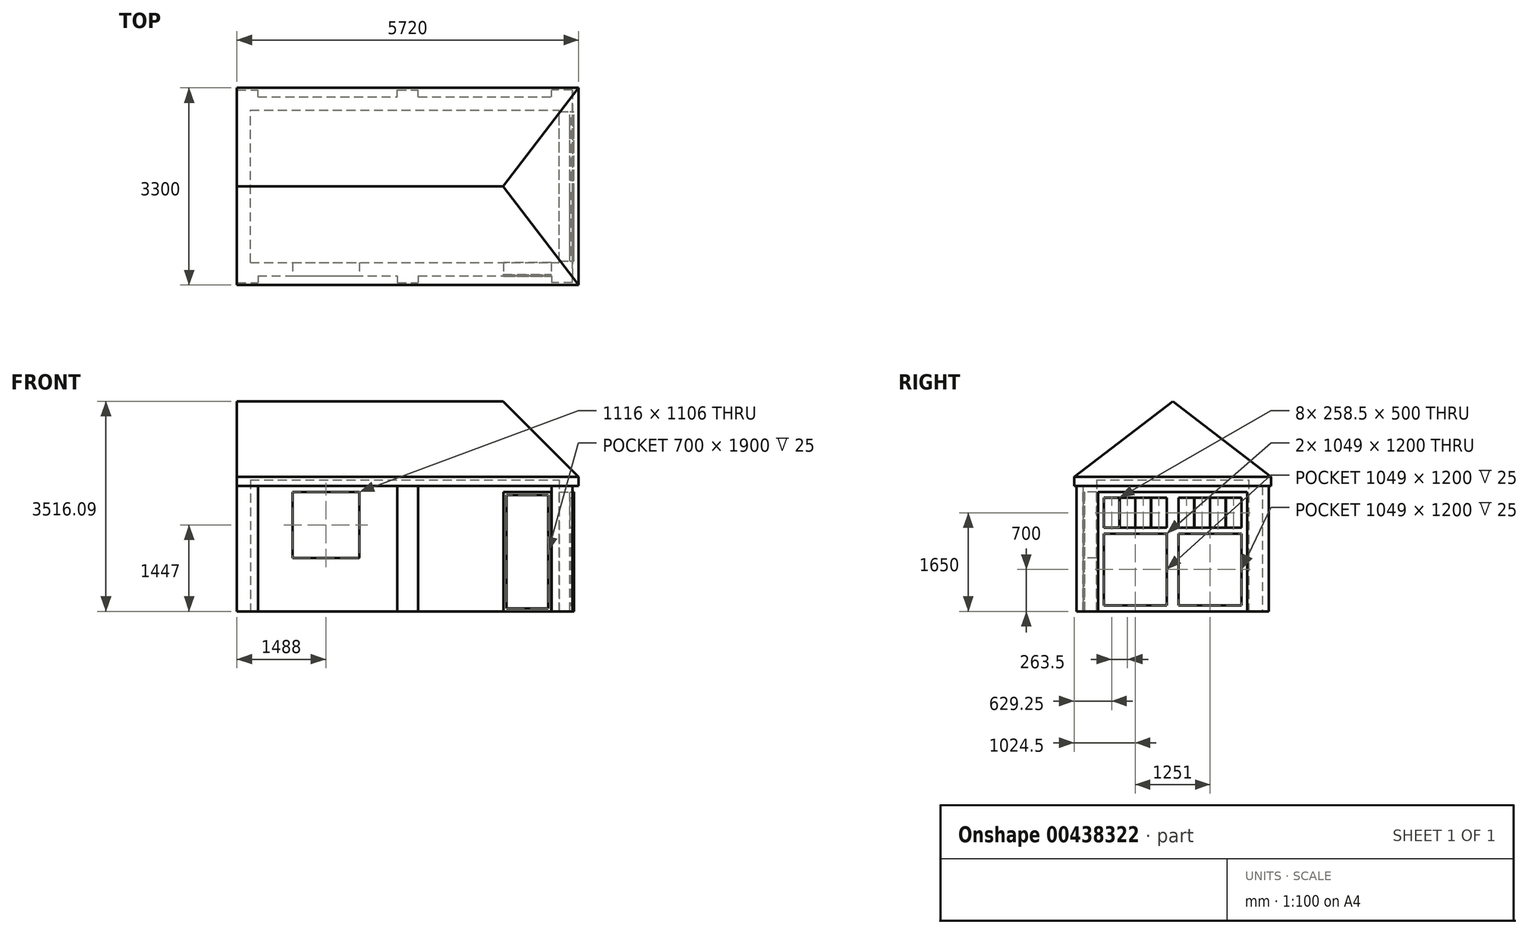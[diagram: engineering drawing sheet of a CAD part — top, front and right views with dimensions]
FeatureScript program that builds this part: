
annotation { "Feature Type Name" : "Feature", "Feature Type Description" : "" }
export const myFeature = defineFeature(function(context is Context, id is Id, definition is map)
    precondition{}
    {
        {
            var Q0;
            Q0=qCreatedBy(makeId("Top.planeOp"),FACE);
            var sketch = newSketch(context, id + "F0", { "sketchPlane" : qUnion([Q0])});
            skLineSegment(sketch, "E0.bottom", {"start": v(0, 0) * mm, "end": v(5620, 0) * mm});
            skLineSegment(sketch, "E0.top", {"start": v(0, 3000) * mm, "end": v(5620, 3000) * mm});
            skLineSegment(sketch, "E0.left", {"start": v(0, 0) * mm, "end": v(0, 3000) * mm});
            skLineSegment(sketch, "E0.right", {"start": v(5620, 0) * mm, "end": v(5620, 3000) * mm});
            skLineSegment(sketch, "E1.bottom", {"start": v(225, 225) * mm, "end": v(5395, 225) * mm});
            skLineSegment(sketch, "E1.top", {"start": v(225, 2775) * mm, "end": v(5395, 2775) * mm});
            skLineSegment(sketch, "E1.left", {"start": v(225, 225) * mm, "end": v(225, 2775) * mm});
            skLineSegment(sketch, "E1.right", {"start": v(5395, 225) * mm, "end": v(5395, 2775) * mm});
            skSolve(sketch);
        }
        {
            var Q0;
            Q0 = qSketchRegion(id + "F0", true);
            extrude(context, id + "F1", {"entities" : qUnion([Q0]), "depth" : 2200 * mm, "offsetDistance" : 25 * mm});
        }
        {
            var Q0;
            Q0=makeQuery(id+"F1.opExtrude","SWEPT_FACE",FACE,{"disambiguationData":[OSD([sQuery(id+"F0.wireOp",EDGE,"E0.right")])]});
            var sketch = newSketch(context, id + "F2", { "sketchPlane" : qUnion([Q0])});
            skLineSegment(sketch, "E2.bottom", {"start": v(250, 0) * mm, "end": v(2750, 0) * mm});
            skLineSegment(sketch, "E2.top", {"start": v(250, 2000) * mm, "end": v(2750, 2000) * mm});
            skLineSegment(sketch, "E2.left", {"start": v(250, 0) * mm, "end": v(250, 2000) * mm});
            skLineSegment(sketch, "E2.right", {"start": v(2750, 0) * mm, "end": v(2750, 2000) * mm});
            skSolve(sketch);
        }
        {
            var Q0;
            Q0 = qSketchRegion(id + "F2", true);
            extrude(context, id + "F3", {"entities" : qUnion([Q0]), "operationType" : NewBodyOperationType.REMOVE, "endBound" : BoundingType.UP_TO_NEXT, "oppositeDirection" : true, "depth" : 25 * mm, "offsetDistance" : 25 * mm});
        }
        {
            var Q0;
            Q0=makeQuery(id+"F1.opExtrude","SWEPT_FACE",FACE,{"disambiguationData":[OSD([sQuery(id+"F0.wireOp",EDGE,"E0.bottom")])]});
            var sketch = newSketch(context, id + "F4", { "sketchPlane" : qUnion([Q0])});
            skLineSegment(sketch, "E3.bottom", {"start": v(930, 2000) * mm, "end": v(2046, 2000) * mm});
            skLineSegment(sketch, "E3.top", {"start": v(930, 894) * mm, "end": v(2046, 894) * mm});
            skLineSegment(sketch, "E3.left", {"start": v(930, 2000) * mm, "end": v(930, 894) * mm});
            skLineSegment(sketch, "E3.right", {"start": v(2046, 2000) * mm, "end": v(2046, 894) * mm});
            skLineSegment(sketch, "E4.bottom", {"start": v(5260, 0) * mm, "end": v(4460, 0) * mm});
            skLineSegment(sketch, "E4.top", {"start": v(5260, 2000) * mm, "end": v(4460, 2000) * mm});
            skLineSegment(sketch, "E4.left", {"start": v(5260, 0) * mm, "end": v(5260, 2000) * mm});
            skLineSegment(sketch, "E4.right", {"start": v(4460, 0) * mm, "end": v(4460, 2000) * mm});
            skSolve(sketch);
        }
        {
            var Q0;
            Q0 = qSketchRegion(id + "F4", true);
            extrude(context, id + "F5", {"entities" : qUnion([Q0]), "operationType" : NewBodyOperationType.REMOVE, "endBound" : BoundingType.UP_TO_NEXT, "oppositeDirection" : true, "depth" : 25 * mm, "offsetDistance" : 25 * mm});
        }
        {
            var Q0;
            Q0=makeQuery(id+"F1.opExtrude","SWEPT_FACE",FACE,{"disambiguationData":[OSD([sQuery(id+"F0.wireOp",EDGE,"E0.bottom")])]});
            cPlane(context, id + "F6", {"entities" : qUnion([Q0]), "cplaneType" : CPlaneType.OFFSET, "offset" : 25 * mm, "oppositeDirection" : true, "width" : 150 * mm, "height" : 150 * mm});
        }
        {
            var Q0;
            Q0=qCreatedBy(id+"F6.planeOp",FACE);
            var sketch = newSketch(context, id + "F7", { "sketchPlane" : qUnion([Q0])});
            skLineSegment(sketch, "E5.bottom", {"start": v(4510, 1950) * mm, "end": v(5210, 1950) * mm});
            skLineSegment(sketch, "E5.top", {"start": v(4510, 50) * mm, "end": v(5210, 50) * mm});
            skLineSegment(sketch, "E5.left", {"start": v(4510, 1950) * mm, "end": v(4510, 50) * mm});
            skLineSegment(sketch, "E5.right", {"start": v(5210, 1950) * mm, "end": v(5210, 50) * mm});
            skLineSegment(sketch, "E6.bottom", {"start": v(4460, 2000) * mm, "end": v(5260, 2000) * mm});
            skLineSegment(sketch, "E6.top", {"start": v(4460, 0) * mm, "end": v(5260, 0) * mm});
            skLineSegment(sketch, "E6.left", {"start": v(4460, 2000) * mm, "end": v(4460, 0) * mm});
            skLineSegment(sketch, "E6.right", {"start": v(5260, 2000) * mm, "end": v(5260, 0) * mm});
            skSolve(sketch);
        }
        {
            var Q0;
            Q0 = qSketchRegion(id + "F7", true);
            extrude(context, id + "F8", {"entities" : qUnion([Q0]), "depth" : 30 * mm, "offsetDistance" : 25 * mm});
        }
        {
            var Q0;
            Q0=makeQuery(id+"F7.imprint","IMPRINT",FACE,{"disambiguationData":[TD([[makeQuery(id+"F7.imprint","IMPRINT",EDGE,{"derivedFrom":sQuery(id+"F7.wireOp",EDGE,"E5.bottom")}),-1.0]])]});
            extrude(context, id + "F9", {"entities" : qUnion([Q0]), "operationType" : NewBodyOperationType.ADD, "depth" : 5 * mm, "offsetDistance" : 25 * mm});
        }
        {
            var Q0;
            Q0=makeQuery(id+"F1.opExtrude","SWEPT_FACE",FACE,{"disambiguationData":[OSD([sQuery(id+"F0.wireOp",EDGE,"E0.right")])]});
            var sketch = newSketch(context, id + "F10", { "sketchPlane" : qUnion([Q0])});
            skLineSegment(sketch, "E7", {"start": v(0, 2100) * mm, "end": v(-150, 2100) * mm});
            skLineSegment(sketch, "E8", {"start": v(-150, 2100) * mm, "end": v(-150, 2250) * mm});
            skLineSegment(sketch, "E9", {"start": v(-150, 2250) * mm, "end": v(1500, 3516.09) * mm});
            skLineSegment(sketch, "E10", {"start": v(1500, 3516.09) * mm, "end": v(3150, 2250) * mm});
            skLineSegment(sketch, "E11", {"start": v(3150, 2250) * mm, "end": v(3150, 2100) * mm});
            skLineSegment(sketch, "E12", {"start": v(3150, 2100) * mm, "end": v(3000, 2100) * mm});
            skLineSegment(sketch, "E13", {"start": v(3000, 2100) * mm, "end": v(3000, 2200) * mm});
            skLineSegment(sketch, "E14", {"start": v(3000, 2200) * mm, "end": v(0, 2200) * mm});
            skLineSegment(sketch, "E15", {"start": v(0, 2200) * mm, "end": v(0, 2100) * mm});
            skSolve(sketch);
        }
        {
            var Q0;
            Q0 = qSketchRegion(id + "F10", true);
            var Q1;
            Q1=makeQuery(id+"F1.opExtrude","SWEPT_FACE",FACE,{"disambiguationData":[OSD([sQuery(id+"F0.wireOp",EDGE,"E0.left")])]});
            extrude(context, id + "F11", {"entities" : qUnion([Q0]), "operationType" : NewBodyOperationType.ADD, "endBound" : BoundingType.UP_TO_SURFACE, "oppositeDirection" : true, "depth" : 5630 * mm, "endBoundEntityFace" : qUnion([Q1]), "offsetDistance" : 100 * mm, "offsetOppositeDirection" : true, "hasSecondDirection" : true, "secondDirectionOppositeDirection" : false, "secondDirectionDepth" : 100 * mm});
        }
        {
            var Q0;
            {var subQ1=sQuery(id+"F10.wireOp",EDGE,"E14");Q0=makeQuery(id+"F11.boolean.opBoolean","SPLIT",FACE,{"disambiguationData":[TD([makeQuery(id+"F1.opExtrude","SWEPT_FACE",FACE,{"disambiguationData":[OSD([sQuery(id+"F0.wireOp",EDGE,"E0.right")])]})])],"derivedFrom":makeQuery(id+"F11.opExtrude","SWEPT_FACE",FACE,{"disambiguationData":[OSD([subQ1])]})});}
            var Q1;
            Q1=makeQuery(id+"F11.opExtrude","SWEPT_FACE",FACE,{"disambiguationData":[OSD([sQuery(id+"F10.wireOp",EDGE,"E7")])]});
            extrude(context, id + "F12", {"entities" : qUnion([Q0]), "operationType" : NewBodyOperationType.ADD, "endBound" : BoundingType.UP_TO_SURFACE, "depth" : 25 * mm, "endBoundEntityFace" : qUnion([Q1]), "offsetDistance" : 25 * mm});
        }
        {
            var Q0;
            Q0=makeQuery(id+"F11.opExtrude","SWEPT_FACE",FACE,{"disambiguationData":[OSD([sQuery(id+"F10.wireOp",EDGE,"E8")])]});
            var sketch = newSketch(context, id + "F13", { "sketchPlane" : qUnion([Q0])});
            skLineSegment(sketch, "E16", {"start": v(5720, 2250) * mm, "end": v(3720, 4250) * mm});
            skLineSegment(sketch, "E17", {"start": v(3720, 4250) * mm, "end": v(5720, 4250) * mm});
            skLineSegment(sketch, "E18", {"start": v(5720, 4250) * mm, "end": v(5720, 2250) * mm});
            skSolve(sketch);
        }
        {
            var Q0;
            Q0 = qSketchRegion(id + "F13", true);
            extrude(context, id + "F14", {"entities" : qUnion([Q0]), "operationType" : NewBodyOperationType.REMOVE, "oppositeDirection" : true, "depth" : 6760 * mm, "offsetDistance" : 25 * mm});
        }
        {
            var Q0;
            {var subQ0=sQuery(id+"F0.wireOp",EDGE,"E0.left");var subQ1=sQuery(id+"F0.wireOp",EDGE,"E0.top");var subQ2=sQuery(id+"F0.wireOp",EDGE,"E0.right");var subQ3=sQuery(id+"F0.wireOp",EDGE,"E0.bottom");var subQ4=sQuery(id+"F0.wireOp",EDGE,"E1.bottom");var subQ5=sQuery(id+"F0.wireOp",EDGE,"E1.top");var subQ6=sQuery(id+"F0.wireOp",EDGE,"E1.left");var subQ7=sQuery(id+"F0.wireOp",EDGE,"E1.right");Q0=makeQuery(id+"F5.boolean.opBoolean","SPLIT",FACE,{"disambiguationData":[TD([makeQuery(id+"F1.opExtrude","SWEPT_FACE",FACE,{"disambiguationData":[OSD([subQ1])]})])],"derivedFrom":makeQuery(id+"F1.opExtrude","CAP_FACE",FACE,{"disambiguationData":[OSD([subQ3,subQ1,subQ0,subQ2,subQ4,subQ5,subQ6,subQ7])],"isStart":true})});}
            var sketch = newSketch(context, id + "F15", { "sketchPlane" : qUnion([Q0])});
            skLineSegment(sketch, "E19.bottom", {"start": v(0, 0) * mm, "end": v(350, 0) * mm});
            skLineSegment(sketch, "E19.top", {"start": v(0, 110) * mm, "end": v(350, 110) * mm});
            skLineSegment(sketch, "E19.left", {"start": v(0, 0) * mm, "end": v(0, 110) * mm});
            skLineSegment(sketch, "E19.right", {"start": v(350, 0) * mm, "end": v(350, 110) * mm});
            skLineSegment(sketch, "E20.bottom", {"start": v(2685, 0) * mm, "end": v(3035, 0) * mm});
            skLineSegment(sketch, "E20.top", {"start": v(2685, 110) * mm, "end": v(3035, 110) * mm});
            skLineSegment(sketch, "E20.left", {"start": v(2685, 0) * mm, "end": v(2685, 110) * mm});
            skLineSegment(sketch, "E20.right", {"start": v(3035, 0) * mm, "end": v(3035, 110) * mm});
            skLineSegment(sketch, "E21.bottom", {"start": v(5620, 0) * mm, "end": v(5270, 0) * mm});
            skLineSegment(sketch, "E21.top", {"start": v(5620, 110) * mm, "end": v(5270, 110) * mm});
            skLineSegment(sketch, "E21.left", {"start": v(5620, 0) * mm, "end": v(5620, 110) * mm});
            skLineSegment(sketch, "E21.right", {"start": v(5270, 0) * mm, "end": v(5270, 110) * mm});
            skLineSegment(sketch, "E22.bottom", {"start": v(0, -3000) * mm, "end": v(350, -3000) * mm});
            skLineSegment(sketch, "E22.top", {"start": v(0, -3110) * mm, "end": v(350, -3110) * mm});
            skLineSegment(sketch, "E22.left", {"start": v(0, -3000) * mm, "end": v(0, -3110) * mm});
            skLineSegment(sketch, "E22.right", {"start": v(350, -3000) * mm, "end": v(350, -3110) * mm});
            skLineSegment(sketch, "E23.bottom", {"start": v(2685, -3000) * mm, "end": v(3035, -3000) * mm});
            skLineSegment(sketch, "E23.top", {"start": v(2685, -3110) * mm, "end": v(3035, -3110) * mm});
            skLineSegment(sketch, "E23.left", {"start": v(2685, -3000) * mm, "end": v(2685, -3110) * mm});
            skLineSegment(sketch, "E23.right", {"start": v(3035, -3000) * mm, "end": v(3035, -3110) * mm});
            skLineSegment(sketch, "E24.bottom", {"start": v(5620, -3000) * mm, "end": v(5270, -3000) * mm});
            skLineSegment(sketch, "E24.top", {"start": v(5620, -3110) * mm, "end": v(5270, -3110) * mm});
            skLineSegment(sketch, "E24.left", {"start": v(5620, -3000) * mm, "end": v(5620, -3110) * mm});
            skLineSegment(sketch, "E24.right", {"start": v(5270, -3000) * mm, "end": v(5270, -3110) * mm});
            skLineSegment(sketch, "E25", {"start": v(2860, 428.34) * mm, "end": v(2860, -3399.48) * mm, "construction": true});
            skSolve(sketch);
        }
        {
            var Q0;
            Q0 = qSketchRegion(id + "F15", true);
            var Q1;
            {var subQ0=sQuery(id+"F10.wireOp",EDGE,"E7");Q1=makeQuery(id+"F12.boolean.opBoolean","MERGE",FACE,{"derivedFrom":[makeQuery(id+"F11.opExtrude","SWEPT_FACE",FACE,{"disambiguationData":[OSD([subQ0])]}),makeQuery(id+"F11.opExtrude","SWEPT_FACE",FACE,{"disambiguationData":[OSD([sQuery(id+"F10.wireOp",EDGE,"E12")])]}),makeQuery(id+"F12.opExtrude","CAP_FACE",FACE,{"disambiguationData":[OSD([subQ0])],"isStart":false})]});}
            extrude(context, id + "F16", {"entities" : qUnion([Q0]), "operationType" : NewBodyOperationType.ADD, "endBound" : BoundingType.UP_TO_SURFACE, "oppositeDirection" : true, "depth" : 25 * mm, "endBoundEntityFace" : qUnion([Q1]), "offsetDistance" : 25 * mm});
        }
        {
            var Q0;
            Q0=makeQuery(id+"F16.boolean.opBoolean","MERGE",FACE,{"derivedFrom":[makeQuery(id+"F1.opExtrude","SWEPT_FACE",FACE,{"disambiguationData":[OSD([sQuery(id+"F0.wireOp",EDGE,"E0.right")])]}),makeQuery(id+"F16.opExtrude","SWEPT_FACE",FACE,{"disambiguationData":[OSD([sQuery(id+"F15.wireOp",EDGE,"E21.left")])]}),makeQuery(id+"F16.opExtrude","SWEPT_FACE",FACE,{"disambiguationData":[OSD([sQuery(id+"F15.wireOp",EDGE,"E24.left")])]})]});
            var sketch = newSketch(context, id + "F17", { "sketchPlane" : qUnion([Q0])});
            skLineSegment(sketch, "E26.bottom", {"start": v(250, 2000) * mm, "end": v(2750, 2000) * mm});
            skLineSegment(sketch, "E26.top", {"start": v(250, 0) * mm, "end": v(2750, 0) * mm});
            skLineSegment(sketch, "E26.left", {"start": v(250, 2000) * mm, "end": v(250, 0) * mm});
            skLineSegment(sketch, "E26.right", {"start": v(2750, 2000) * mm, "end": v(2750, 0) * mm});
            skLineSegment(sketch, "E27.bottom", {"start": v(350, 1300) * mm, "end": v(1399, 1300) * mm});
            skLineSegment(sketch, "E27.top", {"start": v(350, 100) * mm, "end": v(1399, 100) * mm});
            skLineSegment(sketch, "E27.left", {"start": v(350, 1300) * mm, "end": v(350, 100) * mm});
            skLineSegment(sketch, "E27.right", {"start": v(1399, 1300) * mm, "end": v(1399, 100) * mm});
            skLineSegment(sketch, "E28.bottom", {"start": v(1601, 1300) * mm, "end": v(2650, 1300) * mm});
            skLineSegment(sketch, "E28.top", {"start": v(1601, 100) * mm, "end": v(2650, 100) * mm});
            skLineSegment(sketch, "E28.left", {"start": v(1601, 1300) * mm, "end": v(1601, 100) * mm});
            skLineSegment(sketch, "E28.right", {"start": v(2650, 1300) * mm, "end": v(2650, 100) * mm});
            skLineSegment(sketch, "E29.bottom", {"start": v(350, 1900) * mm, "end": v(608.5, 1900) * mm});
            skLineSegment(sketch, "E29.top", {"start": v(350, 1400) * mm, "end": v(608.5, 1400) * mm});
            skLineSegment(sketch, "E29.left", {"start": v(350, 1900) * mm, "end": v(350, 1400) * mm});
            skLineSegment(sketch, "E29.right", {"start": v(608.5, 1900) * mm, "end": v(608.5, 1400) * mm});
            skLineSegment(sketch, "E30.bottom", {"start": v(613.5, 1900) * mm, "end": v(872, 1900) * mm});
            skLineSegment(sketch, "E30.top", {"start": v(613.5, 1400) * mm, "end": v(872, 1400) * mm});
            skLineSegment(sketch, "E30.left", {"start": v(613.5, 1900) * mm, "end": v(613.5, 1400) * mm});
            skLineSegment(sketch, "E30.right", {"start": v(872, 1900) * mm, "end": v(872, 1400) * mm});
            skLineSegment(sketch, "E31.bottom", {"start": v(877, 1900) * mm, "end": v(1135.5, 1900) * mm});
            skLineSegment(sketch, "E31.top", {"start": v(877, 1400) * mm, "end": v(1135.5, 1400) * mm});
            skLineSegment(sketch, "E31.left", {"start": v(877, 1900) * mm, "end": v(877, 1400) * mm});
            skLineSegment(sketch, "E31.right", {"start": v(1135.5, 1900) * mm, "end": v(1135.5, 1400) * mm});
            skLineSegment(sketch, "E32.bottom", {"start": v(1140.5, 1900) * mm, "end": v(1399, 1900) * mm});
            skLineSegment(sketch, "E32.top", {"start": v(1140.5, 1400) * mm, "end": v(1399, 1400) * mm});
            skLineSegment(sketch, "E32.left", {"start": v(1140.5, 1900) * mm, "end": v(1140.5, 1400) * mm});
            skLineSegment(sketch, "E32.right", {"start": v(1399, 1900) * mm, "end": v(1399, 1400) * mm});
            skLineSegment(sketch, "E33.bottom", {"start": v(1601, 1400) * mm, "end": v(1859.5, 1400) * mm});
            skLineSegment(sketch, "E33.top", {"start": v(1601, 1900) * mm, "end": v(1859.5, 1900) * mm});
            skLineSegment(sketch, "E33.left", {"start": v(1601, 1400) * mm, "end": v(1601, 1900) * mm});
            skLineSegment(sketch, "E33.right", {"start": v(1859.5, 1400) * mm, "end": v(1859.5, 1900) * mm});
            skLineSegment(sketch, "E34.bottom", {"start": v(1864.5, 1900) * mm, "end": v(2123, 1900) * mm});
            skLineSegment(sketch, "E34.top", {"start": v(1864.5, 1400) * mm, "end": v(2123, 1400) * mm});
            skLineSegment(sketch, "E34.left", {"start": v(1864.5, 1900) * mm, "end": v(1864.5, 1400) * mm});
            skLineSegment(sketch, "E34.right", {"start": v(2123, 1900) * mm, "end": v(2123, 1400) * mm});
            skLineSegment(sketch, "E35.bottom", {"start": v(2128, 1900) * mm, "end": v(2386.5, 1900) * mm});
            skLineSegment(sketch, "E35.top", {"start": v(2128, 1400) * mm, "end": v(2386.5, 1400) * mm});
            skLineSegment(sketch, "E35.left", {"start": v(2128, 1900) * mm, "end": v(2128, 1400) * mm});
            skLineSegment(sketch, "E35.right", {"start": v(2386.5, 1900) * mm, "end": v(2386.5, 1400) * mm});
            skLineSegment(sketch, "E36.bottom", {"start": v(2391.5, 1900) * mm, "end": v(2650, 1900) * mm});
            skLineSegment(sketch, "E36.top", {"start": v(2391.5, 1400) * mm, "end": v(2650, 1400) * mm});
            skLineSegment(sketch, "E36.left", {"start": v(2391.5, 1900) * mm, "end": v(2391.5, 1400) * mm});
            skLineSegment(sketch, "E36.right", {"start": v(2650, 1900) * mm, "end": v(2650, 1400) * mm});
            skLineSegment(sketch, "E37.bottom", {"start": v(1501, 2000) * mm, "end": v(1499, 2000) * mm});
            skLineSegment(sketch, "E37.top", {"start": v(1501, 0) * mm, "end": v(1499, 0) * mm});
            skLineSegment(sketch, "E37.left", {"start": v(1501, 2000) * mm, "end": v(1501, 0) * mm});
            skLineSegment(sketch, "E37.right", {"start": v(1499, 2000) * mm, "end": v(1499, 0) * mm});
            skSolve(sketch);
        }
        {
            var Q0;
            Q0 = qSketchRegion(id + "F17", true);
            extrude(context, id + "F18", {"entities" : qUnion([Q0]), "oppositeDirection" : true, "depth" : 50 * mm, "offsetDistance" : 25 * mm, "hasSecondDirection" : true, "secondDirectionOppositeDirection" : false, "secondDirectionDepth" : 25 * mm});
        }
        {
            var Q0;
            Q0=makeQuery(id+"F17.imprint","IMPRINT",FACE,{"disambiguationData":[TD([[makeQuery(id+"F17.imprint","IMPRINT",EDGE,{"derivedFrom":sQuery(id+"F17.wireOp",EDGE,"E27.bottom")}),-1.0]])]});
            var Q1;
            Q1=makeQuery(id+"F17.imprint","IMPRINT",FACE,{"disambiguationData":[TD([[makeQuery(id+"F17.imprint","IMPRINT",EDGE,{"derivedFrom":sQuery(id+"F17.wireOp",EDGE,"E28.bottom")}),-1.0]])]});
            extrude(context, id + "F19", {"entities" : qUnion([Q0, Q1]), "operationType" : NewBodyOperationType.ADD, "oppositeDirection" : true, "depth" : 25 * mm, "offsetDistance" : 25 * mm});
        }
    });
